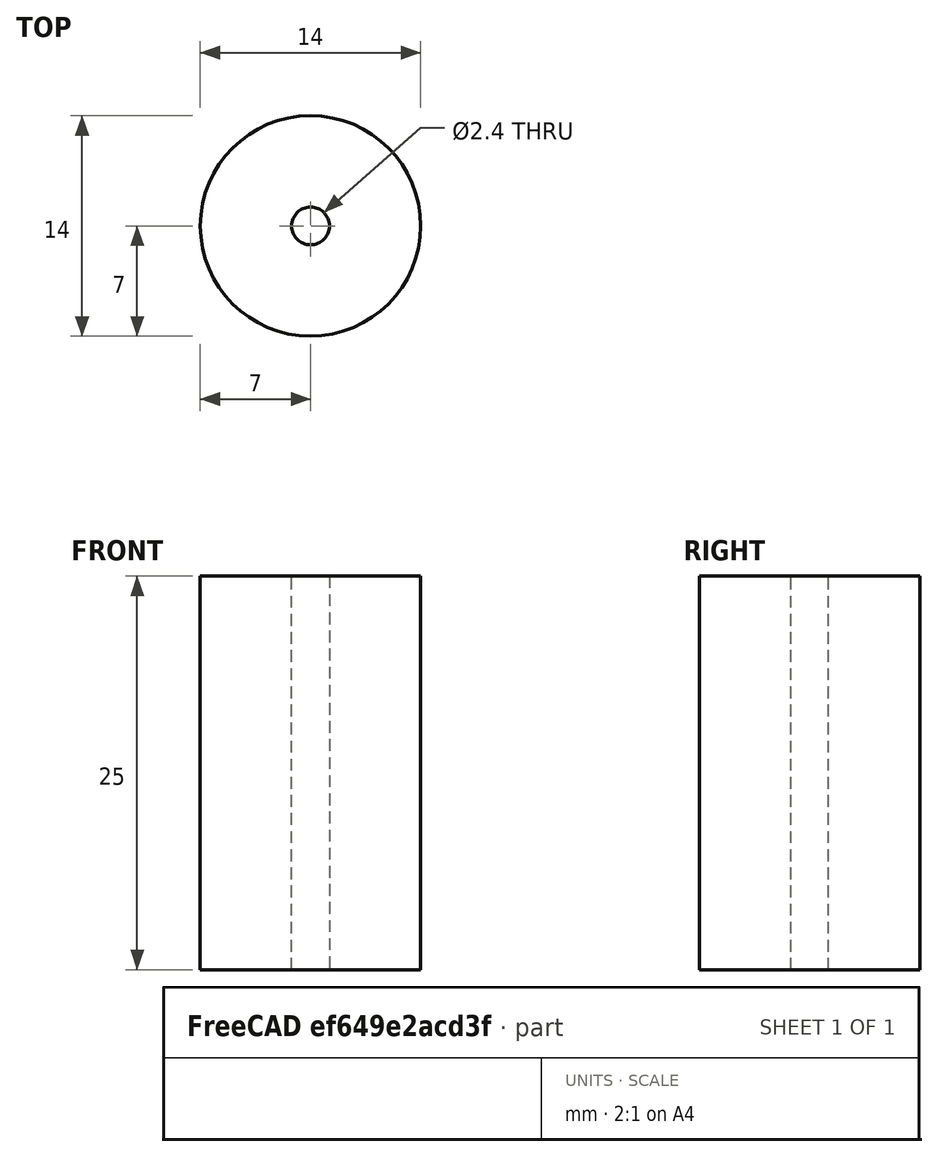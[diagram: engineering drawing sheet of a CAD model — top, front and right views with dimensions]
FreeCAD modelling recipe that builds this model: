
FCSTD DOCUMENT  (FreeCAD 0.21R33668 +26 (Git))
Label: arduino_connector
License: All rights reserved
LicenseURL: https://en.wikipedia.org/wiki/All_rights_reserved
objects: Sketcher::SketchObject×2, PartDesign::Pad×1, PartDesign::Pocket×1, PartDesign::Body×1
note: 7 computed .brp shape members not serialized (recipe doc carries the construction recipe); baked Part::Feature solids carry a one-line shape summary decoded from their .brp

FEATURE [Sketcher::SketchObject] Sketch
  FullyConstrained = false
  MapMode = 5
  Support = -> [XY_Plane]
  sketch-geometry (2):
    g0: Circle CenterX=0 CenterY=0 CenterZ=0 NormalX=0 NormalY=0 NormalZ=1 AngleXU=0 Radius=7
    g1: GeomPoint X=-3.9074 Y=5.80795 Z=0
  constraints (3):
    c: Coincident(g0,g-1)
    c: PointOnObject(g1,g0)
    c: Distance(g1,g0) = 7
FEATURE [PartDesign::Pad] Pad
  Direction = (0,0,1)
  Length = 25
  Length2 = 10
  Profile = -> Sketch
  ReferenceAxis = -> Sketch [N_Axis]
  Type = 0
FEATURE [Sketcher::SketchObject] Sketch001
  FullyConstrained = false
  MapMode = 5
  Placement = pos=(0,0,25) rot=(0,0,1;0rad)
  Support = -> [Pad]
  sketch-geometry (2):
    g0: Circle CenterX=0 CenterY=0 CenterZ=0 NormalX=0 NormalY=0 NormalZ=1 AngleXU=0 Radius=1.2
    g1: GeomPoint X=-0.940143 Y=0.745742 Z=0
  constraints (3):
    c: Coincident(g0,g-1)
    c: PointOnObject(g1,g0)
    c: Distance(g1,g0) = 1.2
FEATURE [PartDesign::Pocket] Pocket
  BaseFeature = -> Pad
  Direction = (0,0,-1)
  Length = 25
  Length2 = 5
  Profile = -> Sketch001
  ReferenceAxis = -> Sketch001 [N_Axis]
  Type = 0
FEATURE [PartDesign::Body] Body
  Group = -> [Sketch,Pad,Sketch001,Pocket]
  Origin = -> Origin
  Tip = -> Pocket
